# Revit family: Afternoon s-045
name_source: partatom
category: Мебель
revit_build: Autodesk Revit 2017 (Build: 20160225_1515(x64)
units: mm (PartAtom-declared; Revit-internal decimal feet)

## family parameters
Всегда вертикально = Да
Заголовок OmniClass = General Furniture and Specialties
На основе рабочей плоскости = Нет
Номер OmniClass = 23.40.20.00
Общий = Нет
При загрузке вырезать с полостями = Нет
Точка расчета площади = Нет

## types (5) — shared parameters
Leg = Skandiform Chrome
Seat = Skandiform Fabric
URL = http://www.biminfo.se
Изготовитель = Skandiform AB
Ключевая пометка = XBF.2
Комментарии к типоразмеру = Created by Astacus AB

## per-type parameters (varying)
| type | Type | Описание |
| S-045 | S-045 | Bar stool in black laminate K1015UN. Chassis in chromium. |
| S-054 | S-054 | Chassis in chromium. Armrests in black polyurethan. |
| S-055 | S-045 | Chassis in chromium or silver lacquer. |
| F-154 | KS-154 | Chassis in chromium. Armrests in black polyurethan. |
| KS-155 | KS-155 | Chassis in chromium or silver lacquer. |

note: column(s) folded — value = type name in every type: Группа модели

## geometry (parser evidence)
native form markers: Blend x9, Sweep x16
no freeform markers — native parametric forms only
